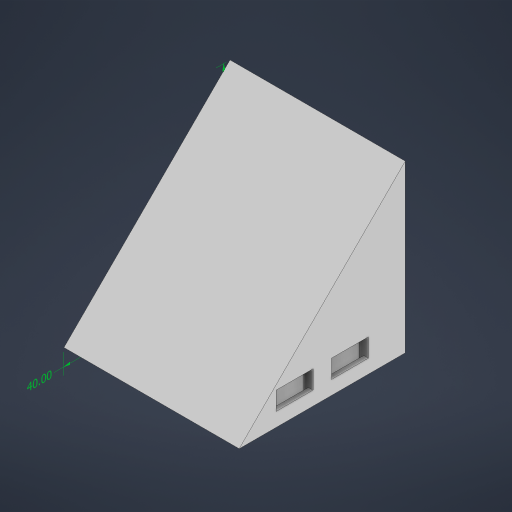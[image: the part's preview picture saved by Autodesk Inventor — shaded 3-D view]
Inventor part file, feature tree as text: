
AUTODESK INVENTOR PART (.ipt)
format: ipt  version: 2024 (Build 280153000, 153)  size: 491,008 bytes
history: native  units: mm
features: other x6, extrude x5, sketch x5
ambient origin geometry x8: Origin, YZ Plane, XZ Plane, XY Plane, X Axis, Y Axis, Z Axis, Center Point
bodies: Body1 (feature_tree)
feature tree (16):
  other  "솔리드1"
  extrude  "돌출1"  Depth=180.0mm
  extrude  "돌출2"  Depth=180.0mm
  extrude  "돌출3"  Depth=190.0mm TaperAngle=0.0deg
  extrude  "돌출4"  Depth=40.0mm
  extrude  "돌출5"  Depth=20.0mm
  sketch  "스케치1"
  sketch  "스케치2"
  sketch  "스케치3"
  sketch  "스케치4"
  sketch  "스케치5"
  other  "선형 치수 1"
  other  "선형 치수 2"
  other  "선형 치수 3"
  other  "선형 치수 4"
  other  "선형 치수 5"
